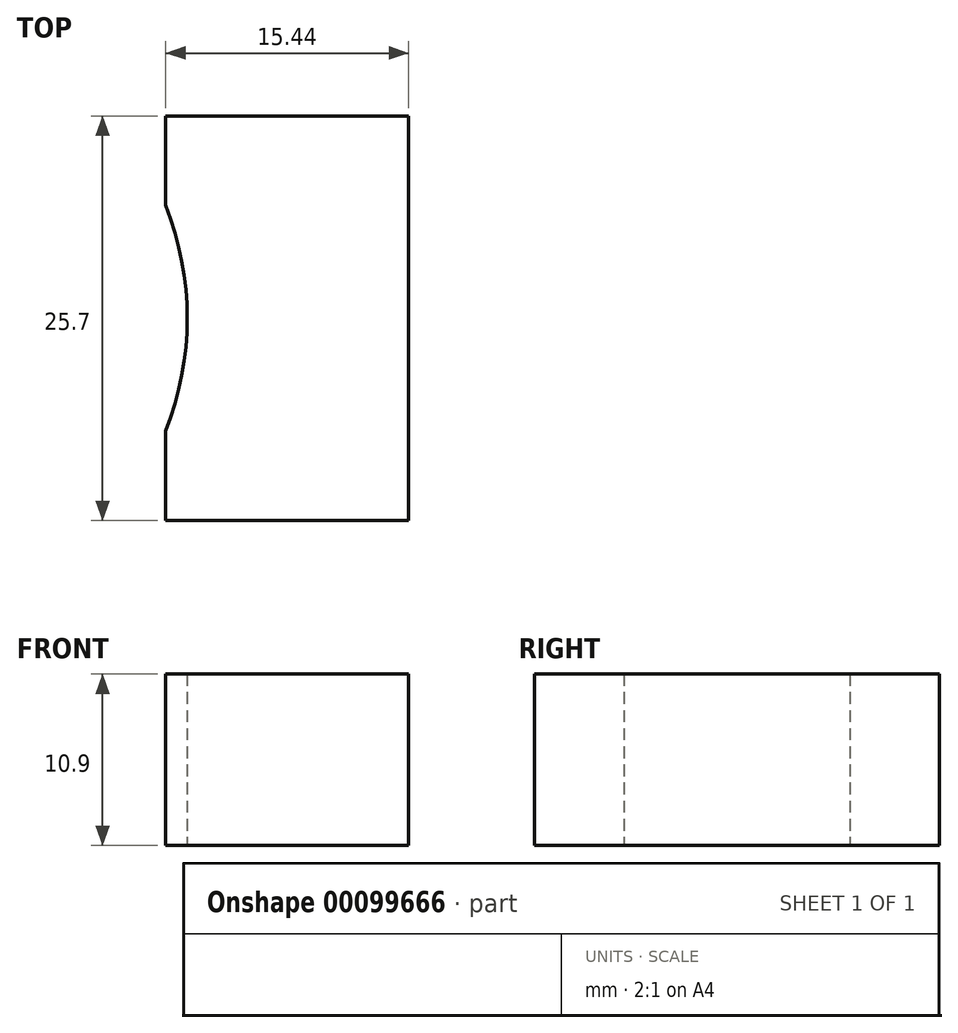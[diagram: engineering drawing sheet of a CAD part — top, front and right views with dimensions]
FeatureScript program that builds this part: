
annotation { "Feature Type Name" : "Feature", "Feature Type Description" : "" }
export const myFeature = defineFeature(function(context is Context, id is Id, definition is map)
    precondition{}
    {
        {
            var Q0;
            Q0=qCreatedBy(makeId("Front.planeOp"),FACE);
            var sketch = newSketch(context, id + "F0", { "sketchPlane" : qUnion([Q0])});
            skLineSegment(sketch, "E0.bottom", {"start": v(-15.44, 10.9) * mm, "end": v(0, 10.9) * mm});
            skLineSegment(sketch, "E0.top", {"start": v(-15.44, 0) * mm, "end": v(0, 0) * mm});
            skLineSegment(sketch, "E0.left", {"start": v(-15.44, 10.9) * mm, "end": v(-15.44, 0) * mm});
            skLineSegment(sketch, "E0.right", {"start": v(0, 10.9) * mm, "end": v(0, 0) * mm});
            skSolve(sketch);
        }
        {
            var Q0;
            Q0=makeQuery(id+"F0.imprint","IMPRINT",FACE,{"disambiguationData":[TD([[makeQuery(id+"F0.imprint","IMPRINT",EDGE,{"derivedFrom":sQuery(id+"F0.wireOp",EDGE,"E0.bottom")}),-1.0]])]});
            extrude(context, id + "F1", {"entities" : qUnion([Q0]), "depth" : 25.7 * mm});
        }
        {
            var Q0;
            Q0=qCreatedBy(makeId("Top.planeOp"),FACE);
            var sketch = newSketch(context, id + "F2", { "sketchPlane" : qUnion([Q0])});
            skCircle(sketch, "E1", {"center": v(-33.57, -12.85) * mm, "radius": 19.5 * mm});
            skLineSegment(sketch, "E2", {"start": v(-7.72, 13.18) * mm, "end": v(-7.72, -31.86) * mm, "construction": true});
            skCircle(sketch, "E3.MirrorC", {"center": v(18.13, -12.85) * mm, "radius": 19.5 * mm});
            skLineSegment(sketch, "E4", {"start": v(-33.57, 6.65) * mm, "end": v(18.13, 6.65) * mm, "construction": true});
            skSolve(sketch);
        }
        {
            var Q0;
            Q0=makeQuery(id+"F2.imprint","IMPRINT",FACE,{"disambiguationData":[TD([[makeQuery(id+"F2.imprint","IMPRINT",EDGE,{"derivedFrom":sQuery(id+"F2.wireOp",EDGE,"E1")}),1.0]])]});
            var Q1;
            Q1=makeQuery(id+"F2.imprint","IMPRINT",FACE,{"disambiguationData":[TD([[makeQuery(id+"F2.imprint","IMPRINT",EDGE,{"derivedFrom":sQuery(id+"F2.wireOp",EDGE,"E3.MirrorC")}),-1.0]])]});
            extrude(context, id + "F3", {"entities" : qUnion([Q0, Q1]), "operationType" : NewBodyOperationType.REMOVE, "endBound" : BoundingType.THROUGH_ALL, "depth" : 10.9 * mm});
        }
        {
            var Q0;
            Q0=makeQuery(id+"F1.opExtrude","CAP_FACE",FACE,{"disambiguationData":[OSD([sQuery(id+"F0.wireOp",EDGE,"E0.bottom"),sQuery(id+"F0.wireOp",EDGE,"E0.top"),sQuery(id+"F0.wireOp",EDGE,"E0.left"),sQuery(id+"F0.wireOp",EDGE,"E0.right")])],"isStart":false});
            var sketch = newSketch(context, id + "F4", { "sketchPlane" : qUnion([Q0])});
            skCircle(sketch, "E5", {"center": v(-9.17, 5.5) * mm, "radius": 4.03 * mm});
            skSolve(sketch);
        }
        {
            var Q0;
            Q0=qCreatedBy(makeId("Front.planeOp"),FACE);
            cPlane(context, id + "F5", {"entities" : qUnion([Q0]), "cplaneType" : CPlaneType.OFFSET, "offset" : 5 * mm, "width" : 150 * mm, "height" : 150 * mm});
        }
    });
